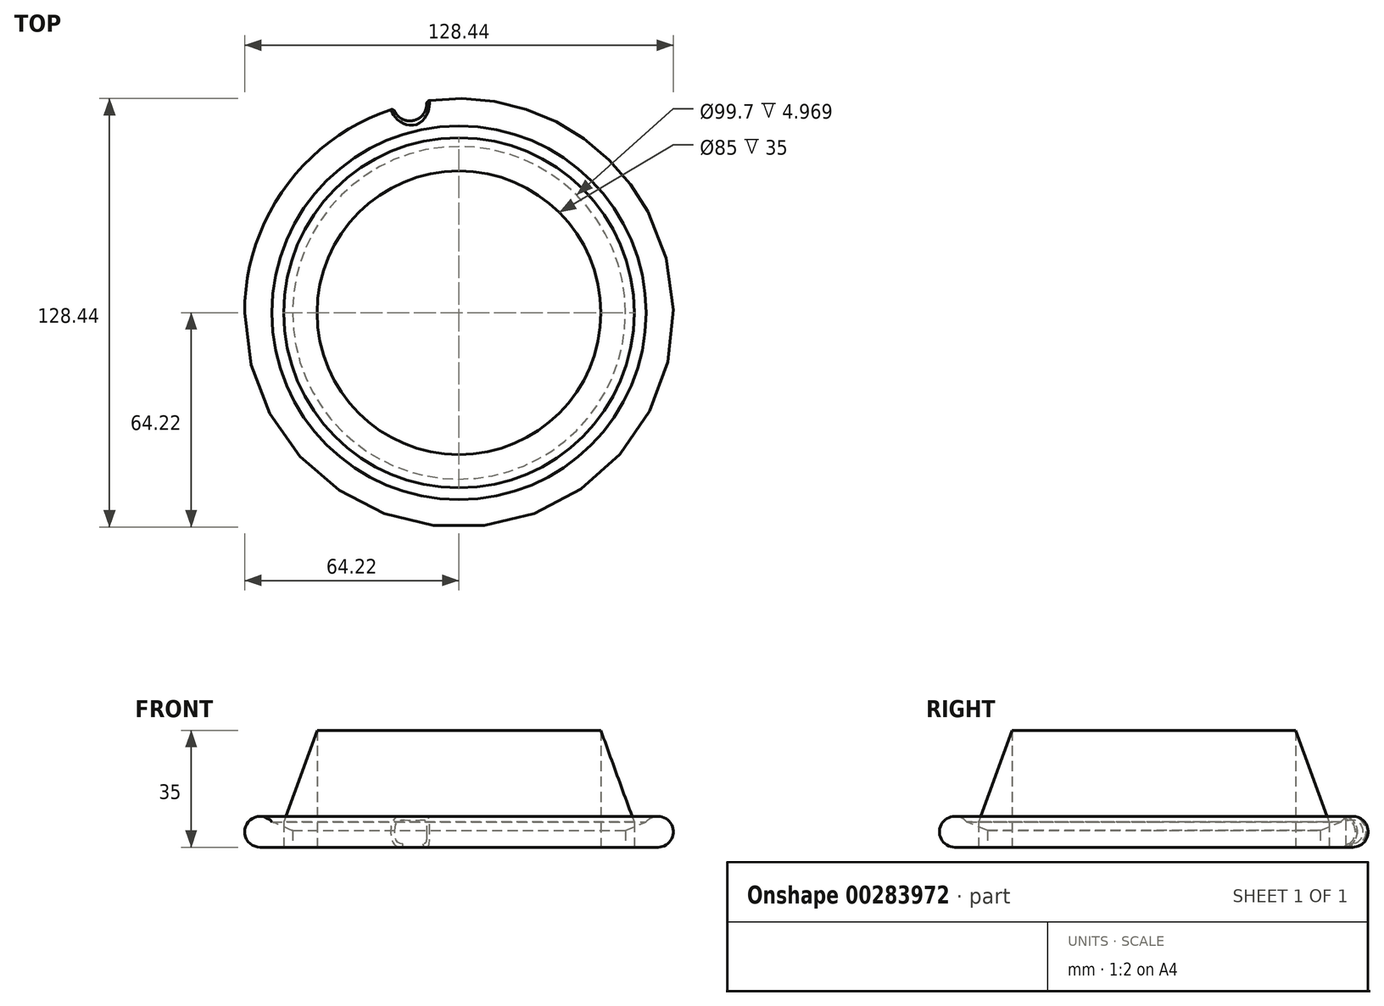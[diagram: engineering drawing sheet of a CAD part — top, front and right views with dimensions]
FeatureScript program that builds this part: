
annotation { "Feature Type Name" : "Feature", "Feature Type Description" : "" }
export const myFeature = defineFeature(function(context is Context, id is Id, definition is map)
    precondition{}
    {
        {
            var Q0;
            Q0=qCreatedBy(makeId("Top.planeOp"),FACE);
            var sketch = newSketch(context, id + "F0", { "sketchPlane" : qUnion([Q0])});
            skCircle(sketch, "E0", {"center": v(0, 0) * mm, "radius": 52.5 * mm});
            skCircle(sketch, "E1.0", {"center": v(0, 0) * mm, "radius": 42.5 * mm});
            skSolve(sketch);
        }
        {
            var Q0;
            Q0=qCreatedBy(makeId("Front.planeOp"),FACE);
            var sketch = newSketch(context, id + "F1", { "sketchPlane" : qUnion([Q0])});
            skLineSegment(sketch, "E2", {"start": v(-49.85, 0) * mm, "end": v(-59.85, 0) * mm});
            skArc(sketch, "E3", {"start": v(-56.03, 7.6) * mm, "mid": v(-63.79, 6.6) * mm, "end": v(-59.6, 0) * mm});
            skLineSegment(sketch, "E4", {"start": v(-56.03, 7.6) * mm, "end": v(-49.85, 4.97) * mm});
            skLineSegment(sketch, "E5", {"start": v(-49.85, 4.97) * mm, "end": v(-49.85, 0) * mm});
            skSolve(sketch);
        }
        {
            var Q0;
            {var subQ2=sQuery(id+"F1.wireOp",EDGE,"E3");Q0=makeQuery(id+"F1.imprint","IMPRINT",FACE,{"disambiguationData":[TD([[makeQuery(id+"F1.imprint","IMPRINT",EDGE,{"derivedFrom":subQ2}),1.0]])]});}
            var Q1;
            Q1=sQuery(id+"F0.wireOp",EDGE,"E1.0");
            revolve(context, id + "F2", {"entities" : qUnion([Q0]), "axis" : qUnion([Q1]), "revolveType" : RevolveType.FULL});
        }
        {
            var Q0;
            Q0=makeQuery(id+"F0.imprint","IMPRINT",FACE,{"disambiguationData":[TD([[makeQuery(id+"F0.imprint","IMPRINT",EDGE,{"derivedFrom":sQuery(id+"F0.wireOp",EDGE,"E0")}),1.0]])]});
            extrude(context, id + "F3", {"entities" : qUnion([Q0]), "depth" : 35 * mm});
        }
        {
            var Q0;
            Q0=makeQuery(id+"F3.opExtrude","CAP_EDGE",EDGE,{"disambiguationData":[OSD([sQuery(id+"F0.wireOp",EDGE,"E0")])],"isStart":false});
            chamfer(context, id + "F4", {"entities" : qUnion([Q0]), "chamferType" : ChamferType.OFFSET_ANGLE, "width" : 10 * mm, "oppositeDirection" : false, "angle" : 70 * degree, "tangentPropagation" : true});
        }
        {
            var Q0;
            Q0=qCreatedBy(makeId("Top.planeOp"),FACE);
            var sketch = newSketch(context, id + "F5", { "sketchPlane" : qUnion([Q0])});
            skCircle(sketch, "E6", {"center": v(-14.7, 62.51) * mm, "radius": 5 * mm});
            skSolve(sketch);
        }
        {
            var Q0;
            Q0=makeQuery(id+"F5.imprint","IMPRINT",FACE,{"disambiguationData":[TD([[makeQuery(id+"F5.imprint","IMPRINT",EDGE,{"derivedFrom":sQuery(id+"F5.wireOp",EDGE,"E6")}),1.0]])]});
            extrude(context, id + "F6", {"entities" : qUnion([Q0]), "operationType" : NewBodyOperationType.REMOVE, "depth" : 25 * mm, "hasSecondDirection" : true, "secondDirectionOppositeDirection" : true, "secondDirectionDepth" : 25 * mm});
        }
        {
            var Q0;
            Q0=makeQuery(id+"F6.boolean.opBoolean","INTERSECT",EDGE,{"derivedFrom":[makeQuery(id+"F2.opRevolve","SWEPT_FACE",FACE,{"disambiguationData":[OSD([sQuery(id+"F1.wireOp",EDGE,"E3")])]}),makeQuery(id+"F6.opExtrude","SWEPT_FACE",FACE,{"disambiguationData":[OSD([sQuery(id+"F5.wireOp",EDGE,"E6")])]})]});
            fillet(context, id + "F7", {"entities" : qUnion([Q0]), "radius" : 1 * mm, "tangentPropagation" : true, "allowEdgeOverflow" : false});
        }
    });
